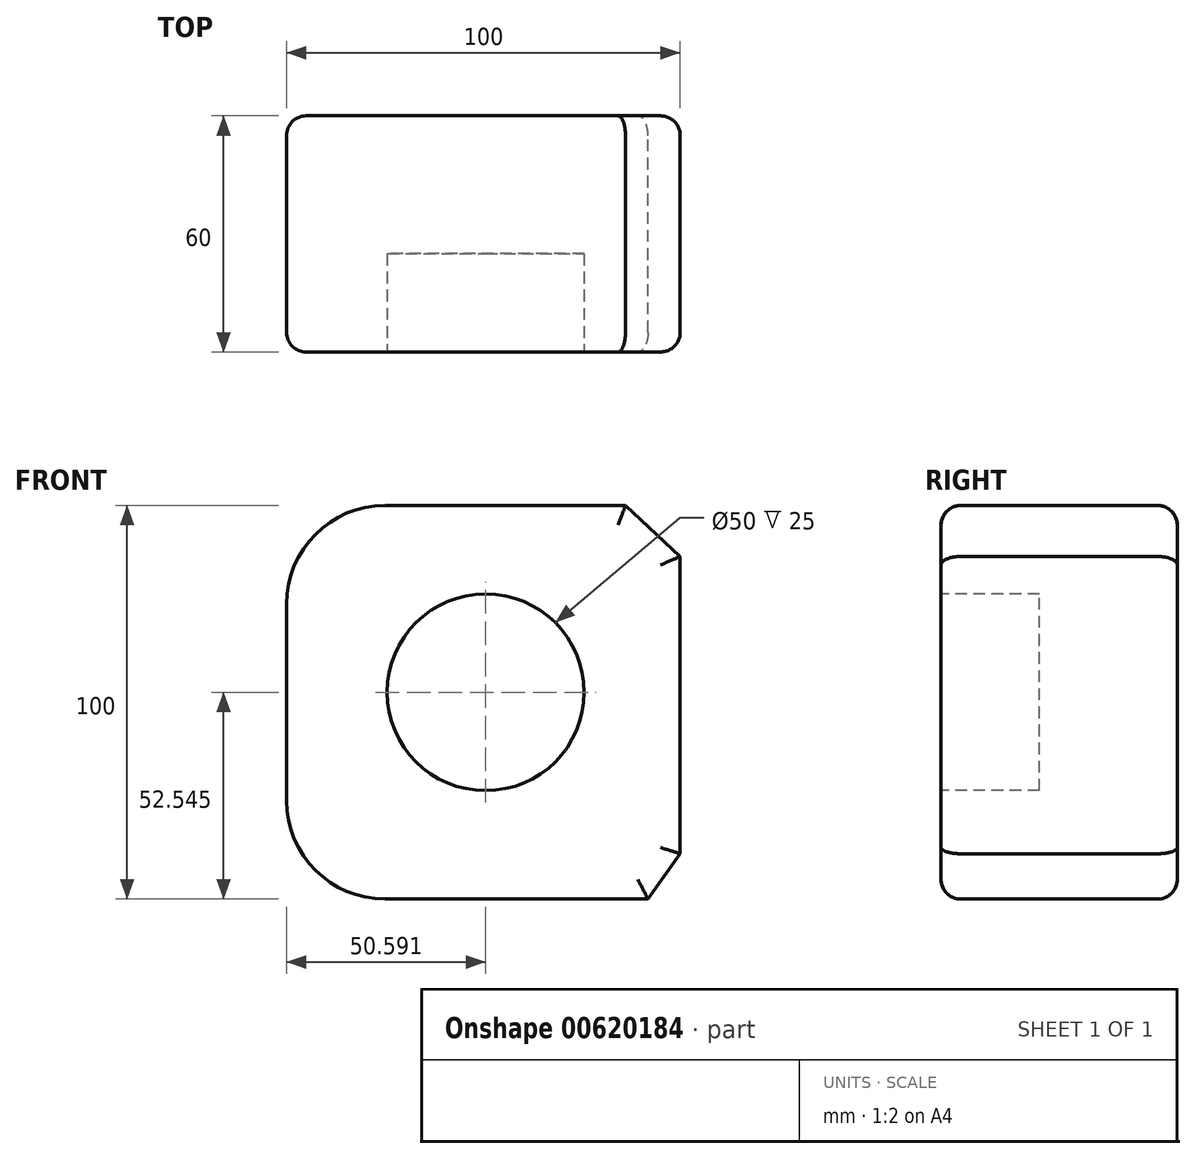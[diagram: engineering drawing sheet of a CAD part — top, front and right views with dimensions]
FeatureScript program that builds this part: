
annotation { "Feature Type Name" : "Feature", "Feature Type Description" : "" }
export const myFeature = defineFeature(function(context is Context, id is Id, definition is map)
    precondition{}
    {
        {
            var Q0;
            Q0=qCreatedBy(makeId("Front.planeOp"),FACE);
            var sketch = newSketch(context, id + "F0", { "sketchPlane" : qUnion([Q0])});
            skLineSegment(sketch, "E0.bottom", {"start": v(-27.65, 53.4) * mm, "end": v(33.47, 53.4) * mm});
            skLineSegment(sketch, "E0.top", {"start": v(-27.65, -46.6) * mm, "end": v(39.18, -46.6) * mm});
            skLineSegment(sketch, "E0.left", {"start": v(-52.65, 28.4) * mm, "end": v(-52.65, -21.6) * mm});
            skLineSegment(sketch, "E0.right", {"start": v(47.35, 40.45) * mm, "end": v(47.35, -35.09) * mm});
            skPoint(sketch, "E1.visualSharp", {"position": v(-52.65, 53.4) * mm});
            skArc(sketch, "E1.filletArc", {"start": v(-27.65, 53.4) * mm, "mid": v(-45.33, 46.08) * mm, "end": v(-52.65, 28.4) * mm});
            skLineSegment(sketch, "E2", {"start": v(33.47, 53.4) * mm, "end": v(47.35, 40.45) * mm});
            skLineSegment(sketch, "E3", {"start": v(39.18, -46.6) * mm, "end": v(47.35, -35.09) * mm});
            skPoint(sketch, "E4.orphan", {"position": v(47.35, 53.4) * mm});
            skPoint(sketch, "E5.visualSharp", {"position": v(-52.65, -46.6) * mm});
            skArc(sketch, "E5.filletArc", {"start": v(-52.65, -21.6) * mm, "mid": v(-45.33, -39.28) * mm, "end": v(-27.65, -46.6) * mm});
            skSolve(sketch);
        }
        {
            var Q0;
            Q0=makeQuery(id+"F0.imprint","IMPRINT",FACE,{"disambiguationData":[TD([[makeQuery(id+"F0.imprint","IMPRINT",EDGE,{"derivedFrom":sQuery(id+"F0.wireOp",EDGE,"E0.bottom")}),-1.0]])]});
            extrude(context, id + "F1", {"entities" : qUnion([Q0]), "depth" : 60 * mm, "offsetDistance" : 25 * mm});
        }
        {
            var Q0;
            Q0=makeQuery(id+"F1.opExtrude","CAP_FACE",FACE,{"disambiguationData":[OSD([sQuery(id+"F0.wireOp",EDGE,"E0.bottom"),sQuery(id+"F0.wireOp",EDGE,"E0.top"),sQuery(id+"F0.wireOp",EDGE,"E0.left"),sQuery(id+"F0.wireOp",EDGE,"E0.right"),sQuery(id+"F0.wireOp",EDGE,"E1.filletArc"),sQuery(id+"F0.wireOp",EDGE,"E2"),sQuery(id+"F0.wireOp",EDGE,"E3"),sQuery(id+"F0.wireOp",EDGE,"E5.filletArc")])],"isStart":false});
            var Q1;
            Q1=makeQuery(id+"F1.opExtrude","CAP_FACE",FACE,{"disambiguationData":[OSD([sQuery(id+"F0.wireOp",EDGE,"E0.bottom"),sQuery(id+"F0.wireOp",EDGE,"E0.top"),sQuery(id+"F0.wireOp",EDGE,"E0.left"),sQuery(id+"F0.wireOp",EDGE,"E0.right"),sQuery(id+"F0.wireOp",EDGE,"E1.filletArc"),sQuery(id+"F0.wireOp",EDGE,"E2"),sQuery(id+"F0.wireOp",EDGE,"E3"),sQuery(id+"F0.wireOp",EDGE,"E5.filletArc")])],"isStart":true});
            fillet(context, id + "F2", {"entities" : qUnion([Q0, Q1]), "radius" : 5 * mm, "tangentPropagation" : true, "allowEdgeOverflow" : false});
        }
        {
            var Q0;
            Q0=makeQuery(id+"F1.opExtrude","CAP_FACE",FACE,{"disambiguationData":[OSD([sQuery(id+"F0.wireOp",EDGE,"E0.bottom"),sQuery(id+"F0.wireOp",EDGE,"E0.top"),sQuery(id+"F0.wireOp",EDGE,"E0.left"),sQuery(id+"F0.wireOp",EDGE,"E0.right"),sQuery(id+"F0.wireOp",EDGE,"E1.filletArc"),sQuery(id+"F0.wireOp",EDGE,"E2"),sQuery(id+"F0.wireOp",EDGE,"E3"),sQuery(id+"F0.wireOp",EDGE,"E5.filletArc")])],"isStart":false});
            var sketch = newSketch(context, id + "F3", { "sketchPlane" : qUnion([Q0])});
            skCircle(sketch, "E6", {"center": v(-2.06, 5.95) * mm, "radius": 25 * mm});
            skSolve(sketch);
        }
        {
            var Q0;
            Q0 = qSketchRegion(id + "F3", true);
            extrude(context, id + "F4", {"entities" : qUnion([Q0]), "operationType" : NewBodyOperationType.REMOVE, "oppositeDirection" : true, "depth" : 25 * mm, "offsetDistance" : 25 * mm});
        }
    });
